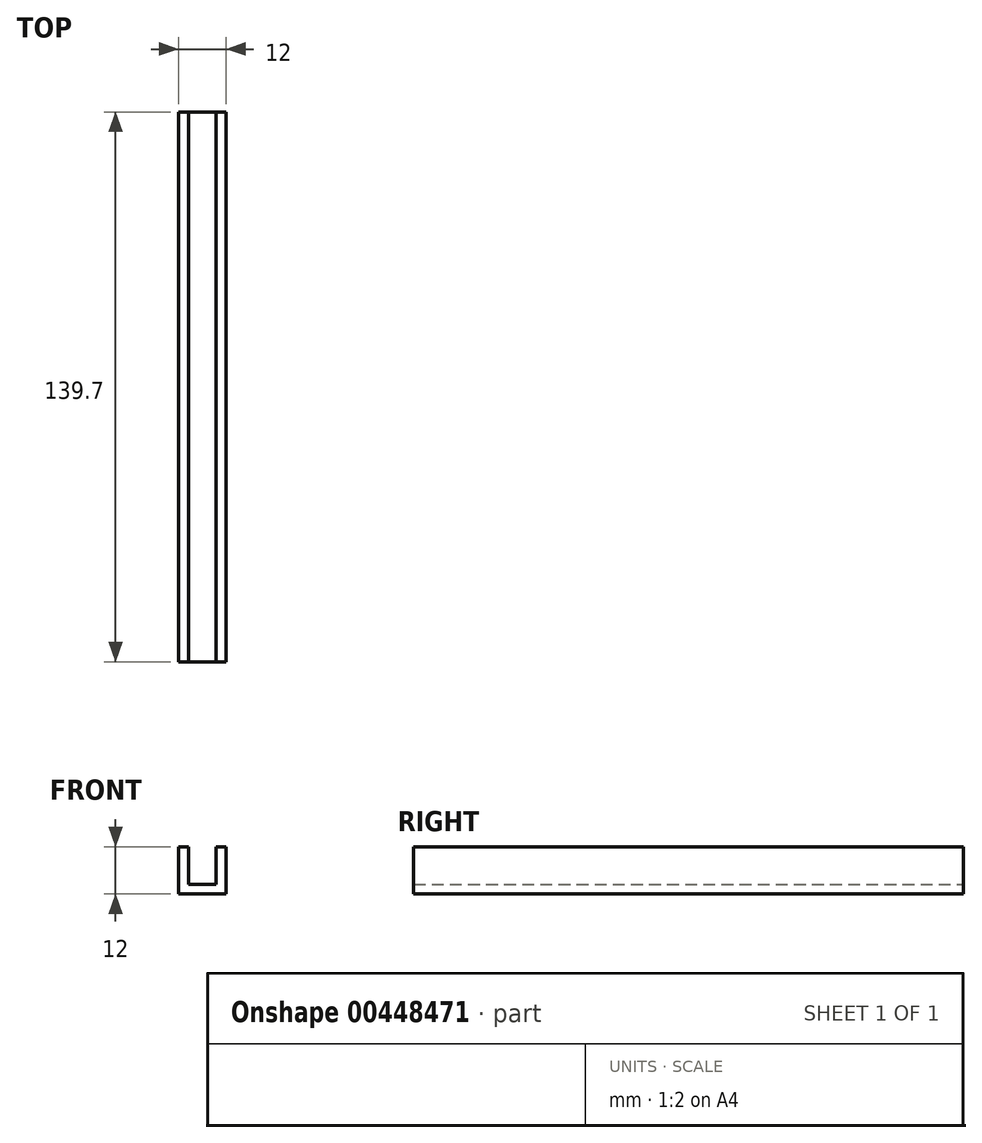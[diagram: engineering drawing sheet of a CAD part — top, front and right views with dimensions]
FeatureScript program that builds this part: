
annotation { "Feature Type Name" : "Feature", "Feature Type Description" : "" }
export const myFeature = defineFeature(function(context is Context, id is Id, definition is map)
    precondition{}
    {
        {
            var Q0;
            Q0=qCreatedBy(makeId("Front.planeOp"),FACE);
            var sketch = newSketch(context, id + "F0", { "sketchPlane" : qUnion([Q0])});
            skLineSegment(sketch, "E0", {"start": v(-6, 0) * mm, "end": v(6, 0) * mm});
            skLineSegment(sketch, "E1", {"start": v(6, 0) * mm, "end": v(6, 12) * mm});
            skLineSegment(sketch, "E2", {"start": v(-6, 0) * mm, "end": v(-6, 12) * mm});
            skLineSegment(sketch, "E3.0", {"start": v(-3.5, 2.5) * mm, "end": v(-3.5, 12) * mm});
            skLineSegment(sketch, "E3.1", {"start": v(-3.5, 2.5) * mm, "end": v(3.5, 2.5) * mm});
            skLineSegment(sketch, "E3.2", {"start": v(3.5, 2.5) * mm, "end": v(3.5, 12) * mm});
            skLineSegment(sketch, "E4", {"start": v(-6, 12) * mm, "end": v(-3.5, 12) * mm});
            skLineSegment(sketch, "E5", {"start": v(3.5, 12) * mm, "end": v(6, 12) * mm});
            skSolve(sketch);
        }
        {
            var Q0;
            Q0=makeQuery(id+"F0.imprint","IMPRINT",FACE,{"disambiguationData":[TD([[makeQuery(id+"F0.imprint","IMPRINT",EDGE,{"derivedFrom":sQuery(id+"F0.wireOp",EDGE,"E0")}),1.0]])]});
            extrude(context, id + "F1", {"entities" : qUnion([Q0]), "endBound" : BoundingType.SYMMETRIC, "depth" : 139.7 * mm});
        }
    });
